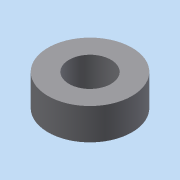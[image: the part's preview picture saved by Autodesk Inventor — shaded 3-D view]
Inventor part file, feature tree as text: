
AUTODESK INVENTOR PART (.ipt)
format: ipt  version: 2015 (Build 190159000, 159)  size: 74,240 bytes
history: native  units: mm
features: extrude x1, sketch x1
ambient origin geometry x8: Origin, YZ Plane, XZ Plane, XY Plane, X Axis, Y Axis, Z Axis, Center Point
bodies: Solid1 (feature_tree)
feature tree (2):
  extrude  "Extrusion1"  Depth=3.0mm
  sketch  "Sketch1"  dims[d0=4.0mm d1=8.0mm d2=3.0mm d3=0.0mm]
